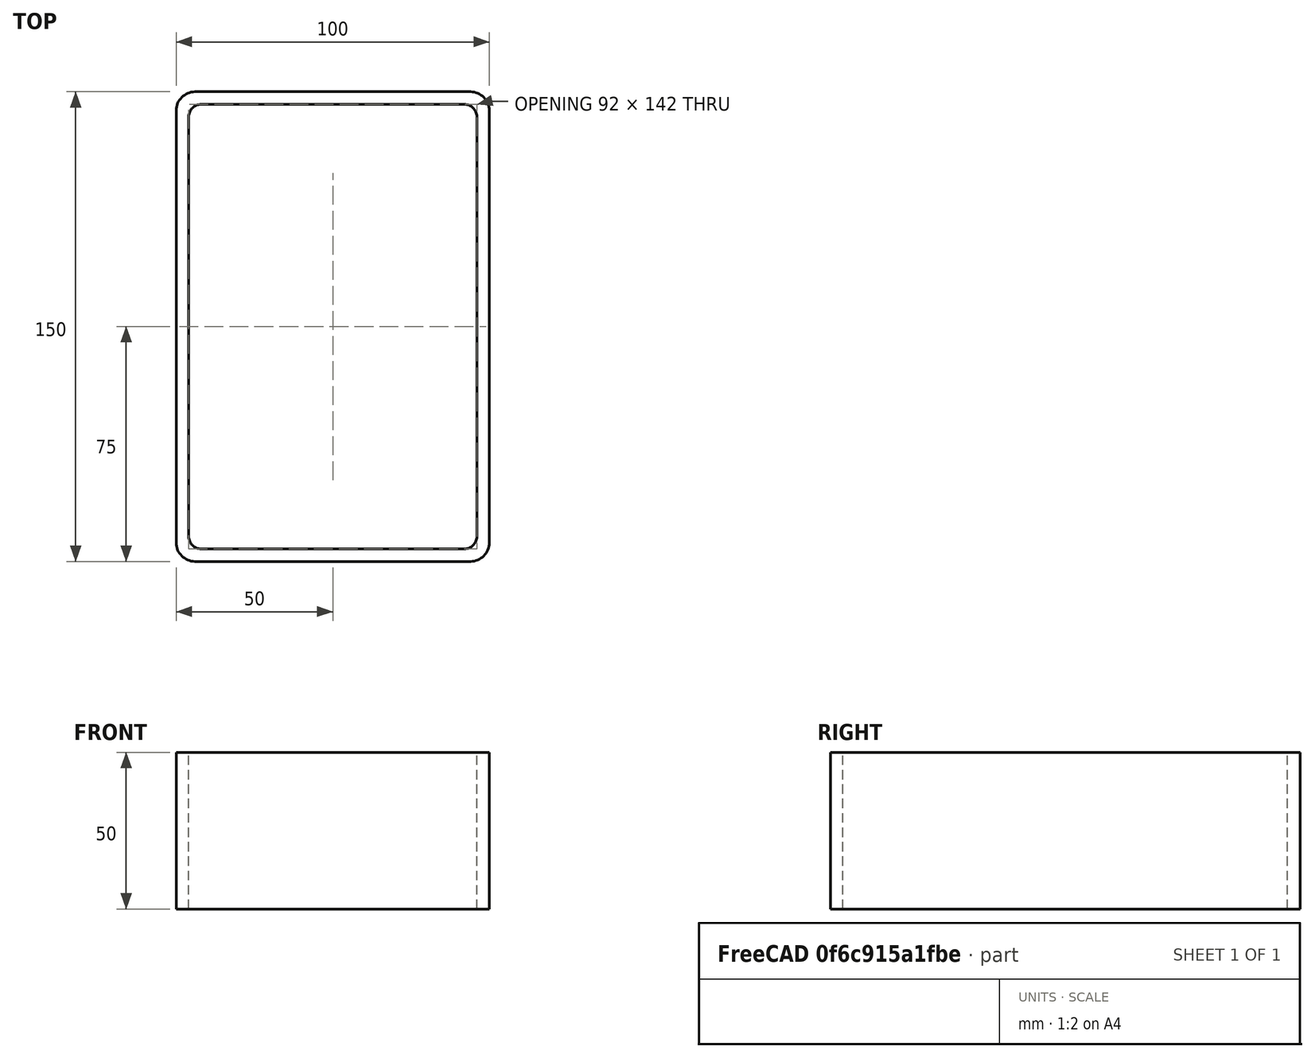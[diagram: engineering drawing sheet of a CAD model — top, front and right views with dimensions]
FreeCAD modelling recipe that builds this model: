
FCSTD DOCUMENT  (FreeCAD 0.15R4671 (Git))
Label: Rectangular hollow section 150x100x4 EN10219 S235JRH
License: All rights reserved
LicenseURL: http://en.wikipedia.org/wiki/All_rights_reserved
objects: Sketcher::SketchObject×1, Part::Extrusion×1
note: 2 computed .brp shape members not serialized (recipe doc carries the construction recipe); baked Part::Feature solids carry a one-line shape summary decoded from their .brp

FEATURE [Sketcher::SketchObject] Sketch
  sketch-geometry (16):
    g0: LineSegment StartX=-42 StartY=71 StartZ=0 EndX=42 EndY=71 EndZ=0
    g1: LineSegment StartX=46 StartY=67 StartZ=0 EndX=46 EndY=-67 EndZ=0
    g2: LineSegment StartX=42 StartY=-71 StartZ=0 EndX=-42 EndY=-71 EndZ=0
    g3: LineSegment StartX=-46 StartY=-67 StartZ=0 EndX=-46 EndY=67 EndZ=0
    g4: LineSegment StartX=-44 StartY=75 StartZ=0 EndX=44 EndY=75 EndZ=0
    g5: LineSegment StartX=50 StartY=69 StartZ=0 EndX=50 EndY=-69 EndZ=0
    g6: LineSegment StartX=44 StartY=-75 StartZ=0 EndX=-44 EndY=-75 EndZ=0
    g7: LineSegment StartX=-50 StartY=-69 StartZ=0 EndX=-50 EndY=69 EndZ=0
    g8: ArcOfCircle CenterX=-42 CenterY=67 CenterZ=0 NormalX=0 NormalY=0 NormalZ=1 Radius=4 StartAngle=1.5708 EndAngle=3.14159
    g9: ArcOfCircle CenterX=42 CenterY=67 CenterZ=0 NormalX=0 NormalY=0 NormalZ=1 Radius=4 StartAngle=0 EndAngle=1.5708
    g10: ArcOfCircle CenterX=42 CenterY=-67 CenterZ=0 NormalX=0 NormalY=0 NormalZ=1 Radius=4 StartAngle=4.71239 EndAngle=6.28319
    g11: ArcOfCircle CenterX=-42 CenterY=-67 CenterZ=0 NormalX=0 NormalY=0 NormalZ=1 Radius=4 StartAngle=3.14159 EndAngle=4.71239
    g12: ArcOfCircle CenterX=44 CenterY=69 CenterZ=0 NormalX=0 NormalY=0 NormalZ=1 Radius=6 StartAngle=0 EndAngle=1.5708
    g13: ArcOfCircle CenterX=44 CenterY=-69 CenterZ=0 NormalX=0 NormalY=0 NormalZ=1 Radius=6 StartAngle=4.71239 EndAngle=6.28319
    g14: ArcOfCircle CenterX=-44 CenterY=-69 CenterZ=0 NormalX=0 NormalY=0 NormalZ=1 Radius=6 StartAngle=3.14159 EndAngle=4.71239
    g15: ArcOfCircle CenterX=-44 CenterY=69 CenterZ=0 NormalX=0 NormalY=0 NormalZ=1 Radius=6 StartAngle=1.5708 EndAngle=3.14159
  constraints (36):
    c: Horizontal(g2)
    c: Vertical(g3)
    c: Horizontal(g6)
    c: Vertical(g7)
    c: Tangent(g3,g8) = 1.5708
    c: Tangent(g0,g8) = 1.5708
    c: Tangent(g0,g9) = 1.5708
    c: Tangent(g1,g9) = 1.5708
    c: Tangent(g1,g10) = 1.5708
    c: Tangent(g2,g10) = 1.5708
    c: Tangent(g2,g11) = 1.5708
    c: Tangent(g3,g11) = 1.5708
    c: Tangent(g4,g12) = 1.5708
    c: Tangent(g5,g12) = 1.5708
    c: Tangent(g5,g13) = 1.5708
    c: Tangent(g6,g13) = 1.5708
    c: Tangent(g6,g14) = 1.5708
    c: Tangent(g7,g14) = 1.5708
    c: Tangent(g7,g15) = 1.5708
    c: Tangent(g4,g15) = 1.5708
    c: Equal(g9,g8)
    c: Equal(g9,g11)
    c: Equal(g9,g10)
    c: Equal(g12,g15)
    c: Equal(g12,g14)
    c: Equal(g12,g13)
    c: Symmetric(g4,g6,g-1)
    c: Symmetric(g7,g5,g-2)
    c: DistanceY(g4,g6) = -150
    c: DistanceX(g7,g5) = 100
    c: Symmetric(g3,g1,g-2)
    c: Symmetric(g0,g2,g-1)
    c: DistanceY(g0,g4) = 4
    c: DistanceX(g5,g1) = -4
    c: Radius(g9) = 4
    c: Radius(g12) = 6
FEATURE [Part::Extrusion] Extrude  label="Rectangular hollow section 150x100x4 EN10219 S235JRH"
  Base = -> Sketch
  Dir = (0,0,50)
  Solid = true
